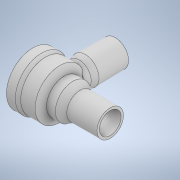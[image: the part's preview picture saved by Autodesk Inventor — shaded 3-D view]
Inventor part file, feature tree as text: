
AUTODESK INVENTOR PART (.ipt)
format: ipt  version: 2020 (Build 240168000, 168)  size: 840,192 bytes
history: native  units: mm
features: sketch x13, extrude x7, revolve x5, plane x4, projected_geometry x2, thread x1, helix x1, other x1
ambient origin geometry x8: Origin, YZ Plane, XZ Plane, XY Plane, X Axis, Y Axis, Z Axis, Center Point
bodies: Solid1 (feature_tree), Solid2 (feature_tree)
feature tree (34):
  revolve  "Revolution1"  [1 undecoded]
  thread  "Thread1"  [1 undecoded]
  revolve  "Revolution2"  [1 undecoded]
  helix  "Coil1"  [1 undecoded]
  plane  "Work Plane1"
  extrude  "Extrusion1"  Depth=17.95mm
  extrude  "Extrusion2"  Depth=17.95mm
  plane  "Work Plane2"
  extrude  "Extrusion3"  Depth=20.5mm
  extrude  "Extrusion4"  TaperAngle=0.0deg  [1 undecoded]
  extrude  "Extrusion5"  Depth=21.8mm
  extrude  "Extrusion6"  Depth=10.5mm
  other  "Work Axis1"
  revolve  "Revolution3"  Angle=90.0deg
  revolve  "Revolution4"  [1 undecoded]
  plane  "Work Plane3"
  revolve  "Revolution5"  [1 undecoded]
  plane  "Work Plane4"
  extrude  "Extrusion7"  Depth=1.5mm
  sketch  "Sketch1"  dims[d0=25.0mm d1=11.0mm d2=11.25mm]
  sketch  "Sketch2"  dims[d3=9.0mm d10=20.5mm d12=120.0deg]
  sketch  "Sketch3"  dims[d13=0.0mm d14=17.95mm]
  sketch  "Sketch4"  dims[d15=17.95mm d16=16.0mm]
  sketch  "Sketch5"  dims[d17=17.0mm d18=20.5mm]
  sketch  "Sketch6"  dims[d19=12.0mm d20=0.0mm]
  sketch  "Sketch7"  dims[d21=20.0mm d23=21.8mm]
  sketch  "Sketch8"  dims[d24=3.0mm d25=10.5mm]
  sketch  "Sketch9"  dims[d26=0.0mm d27=90.0deg]
  sketch  "Sketch10"  dims[d28=2.0mm d29=2.0mm]
  sketch  "Sketch11"  dims[d30=2.0mm d31=7.0mm d32=1.5mm]
  projected_geometry  "Projected Loop1"
  sketch  "Sketch13"  dims[d33=9.599311mm d34=0.240125mm d35=0.240125mm d38=1.5mm]
  projected_geometry  "Projected Loop2"
  sketch  "Sketch15"  dims[d40=9.599311mm d42=0.0mm d43=1.5015mm d44=10.0mm d45=10.0mm d46=0.0mm d47=0.0mm d48=0.0mm d49=0.0mm d50=0.0mm d51=-15.164mm d52=3.5mm d53=8.0mm d54=2.0mm d55=2.0mm d56=3.0mm d57=0.0mm d58=6.5mm d59=2.0mm d60=0.0mm d61=20.5mm d63=12.5mm d64=7.0mm d65=10.0mm d66=0.0mm d67=15.0mm d68=7.0mm d69=0.0mm d70=3.5mm d71=7.0mm d72=3.5mm d73=20.0mm d74=2.0mm d75=0.0mm d76=2.5mm d77=0.0mm d78=1.0mm d79=0.0mm d81=9.0mm d82=11.5mm d83=11.0mm d84=25.0mm d85=0.0mm d86=90.0deg d87=5.0mm d88=90.0deg d89=90.0deg d90=-50.0mm d91=80.0mm d92=0.0mm]
note: 7 required parameter values undecoded (feature->parameter linkage not recoverable at this tier; creation-order binding heuristic only, values carry confidence <= 0.55)